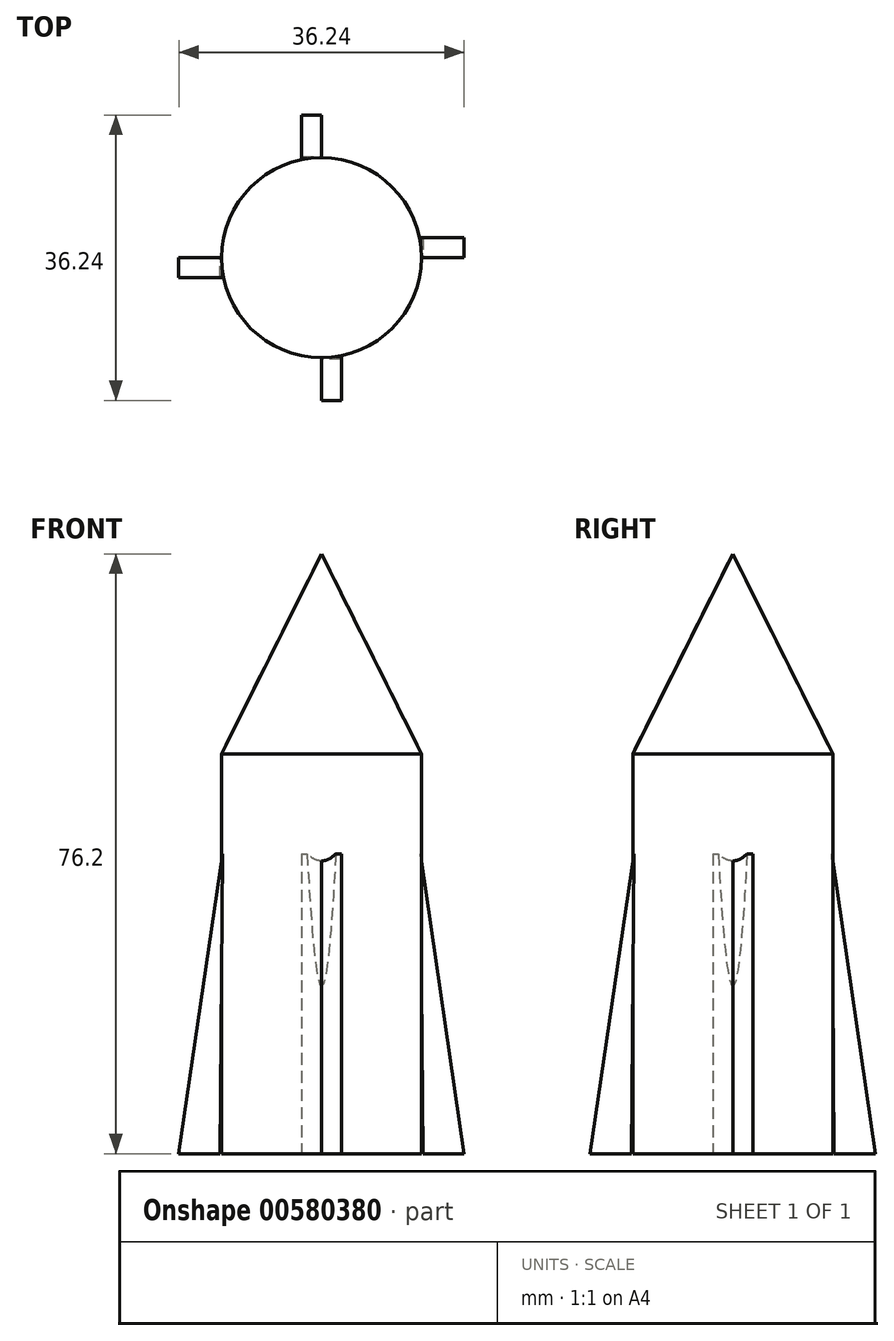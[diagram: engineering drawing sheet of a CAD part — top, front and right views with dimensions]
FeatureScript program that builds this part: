
annotation { "Feature Type Name" : "Feature", "Feature Type Description" : "" }
export const myFeature = defineFeature(function(context is Context, id is Id, definition is map)
    precondition{}
    {
        {
            var Q0;
            Q0=qCreatedBy(makeId("Front.planeOp"),FACE);
            var sketch = newSketch(context, id + "F0", { "sketchPlane" : qUnion([Q0])});
            skLineSegment(sketch, "E0", {"start": v(0, 0) * mm, "end": v(12.7, 0) * mm});
            skLineSegment(sketch, "E1", {"start": v(12.7, 0) * mm, "end": v(12.7, 50.8) * mm});
            skLineSegment(sketch, "E2", {"start": v(12.7, 50.8) * mm, "end": v(0, 76.2) * mm});
            skLineSegment(sketch, "E3", {"start": v(0, 76.2) * mm, "end": v(0, 0) * mm});
            skLineSegment(sketch, "E4", {"start": v(12.7, 22.92) * mm, "end": v(18.3, 0) * mm});
            skLineSegment(sketch, "E5", {"start": v(12.7, 0) * mm, "end": v(12.7, 22.92) * mm});
            skLineSegment(sketch, "E6", {"start": v(18.3, 0) * mm, "end": v(12.7, 0) * mm});
            skSolve(sketch);
        }
        {
            var Q0;
            Q0=makeQuery(id+"F0.imprint","IMPRINT",FACE,{"disambiguationData":[TD([[makeQuery(id+"F0.imprint","IMPRINT",EDGE,{"derivedFrom":sQuery(id+"F0.wireOp",EDGE,"E0")}),1.0]])]});
            var Q1;
            Q1=sQuery(id+"F0.wireOp",EDGE,"E3");
            revolve(context, id + "F1", {"entities" : qUnion([Q0]), "axis" : qUnion([Q1]), "revolveType" : RevolveType.FULL});
        }
        {
            var Q0;
            Q0=qCreatedBy(makeId("Front.planeOp"),FACE);
            var sketch = newSketch(context, id + "F2", { "sketchPlane" : qUnion([Q0])});
            skLineSegment(sketch, "E7", {"start": v(12.87, 0) * mm, "end": v(18.12, 0) * mm});
            skLineSegment(sketch, "E8", {"start": v(18.12, 0) * mm, "end": v(12.57, 38.1) * mm});
            skLineSegment(sketch, "E9", {"start": v(12.57, 38.1) * mm, "end": v(12.87, 0) * mm});
            skSolve(sketch);
        }
        {
            var Q0;
            Q0=makeQuery(id+"F2.imprint","IMPRINT",FACE,{"disambiguationData":[TD([[makeQuery(id+"F2.imprint","IMPRINT",EDGE,{"derivedFrom":sQuery(id+"F2.wireOp",EDGE,"E7")}),1.0]])]});
            var Q1;
            Q1 = qConstructionFilter(qBodyType(qCreatedBy(id + "F2" ,EDGE), BodyType.WIRE), ConstructionObject.NO);
            extrude(context, id + "F3", {"entities" : qUnion([Q0]), "operationType" : NewBodyOperationType.ADD, "surfaceEntities" : qUnion([Q1]), "oppositeDirection" : true, "depth" : 2.54 * mm, "offsetDistance" : 25.4 * mm});
        }
        {
            var Q0;
            Q0=qCreatedBy(makeId("Front.planeOp"),FACE);
            var sketch = newSketch(context, id + "F4", { "sketchPlane" : qUnion([Q0])});
            skLineSegment(sketch, "E10", {"start": v(0, -17.13) * mm, "end": v(0, 78.77) * mm, "construction": true});
            skSolve(sketch);
        }
        {
            var Q0;
            Q0=makeQuery(id+"F1.opRevolve","SWEPT_BODY",BODY,{"disambiguationData":[OSD([sQuery(id+"F0.wireOp",EDGE,"E0"),sQuery(id+"F0.wireOp",EDGE,"E1"),sQuery(id+"F0.wireOp",EDGE,"E2"),sQuery(id+"F0.wireOp",EDGE,"E3"),sQuery(id+"F0.wireOp",EDGE,"E5")])]});
            var Q1;
            Q1=sQuery(id+"F4.wireOp",EDGE,"E10");
            circularPattern(context, id + "F5", {"entities" : qUnion([Q0]), "axis" : qUnion([Q1]), "angle" : 360 * degree, "instanceCount" : 4, "equalSpace" : true});
        }
    });
